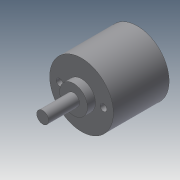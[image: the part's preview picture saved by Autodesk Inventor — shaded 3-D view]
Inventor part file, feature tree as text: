
AUTODESK INVENTOR PART (.ipt)
format: ipt  version: 2014 SP1 (Build 180222100, 222)  size: 146,944 bytes
history: native  units: in
note: dims shown in document units (in); Inventor stores cm internally (conversion verified against a paired STEP export)
features: extrude x6, sketch x6, fillet x1
ambient origin geometry x8: Origin, YZ Plane, XZ Plane, XY Plane, X Axis, Y Axis, Z Axis, Center Point
bodies: Solid1 (feature_tree)
feature tree (13):
  extrude  "Extrusion1"  Depth=0.5512in TaperAngle=0.0deg
  extrude  "Extrusion2"  Depth=0.0669in
  extrude  "Extrusion3"  Depth=0.2165in
  extrude  "Extrusion4"  Depth=0.3937in
  extrude  "Extrusion5"  Depth=0.1181in
  fillet  "Fillet1"  Radius=0.3051in
  extrude  "Extrusion6"  Depth=0.0197in
  sketch  "Sketch1"  dims[d0=0.6299in d1=0.5512in d2=0.0in]
  sketch  "Sketch2"  dims[d3=0.0669in d4=0.0669in]
  sketch  "Sketch3"  dims[d5=0.2165in d6=0.2165in]
  sketch  "Sketch4"  dims[d7=0.3937in d8=0.0in d9=0.2756in]
  sketch  "Sketch5"  dims[d10=0.0787in d11=0.0in d12=0.1181in d13=0.3051in d14=0.0in]
  sketch  "Sketch6"  dims[d15=0.6004in d16=0.2323in d17=0.2323in d18=0.7244in d19=0.0in d20=0.0197in d21=0.1969in d22=0.0197in d23=0.0in]
